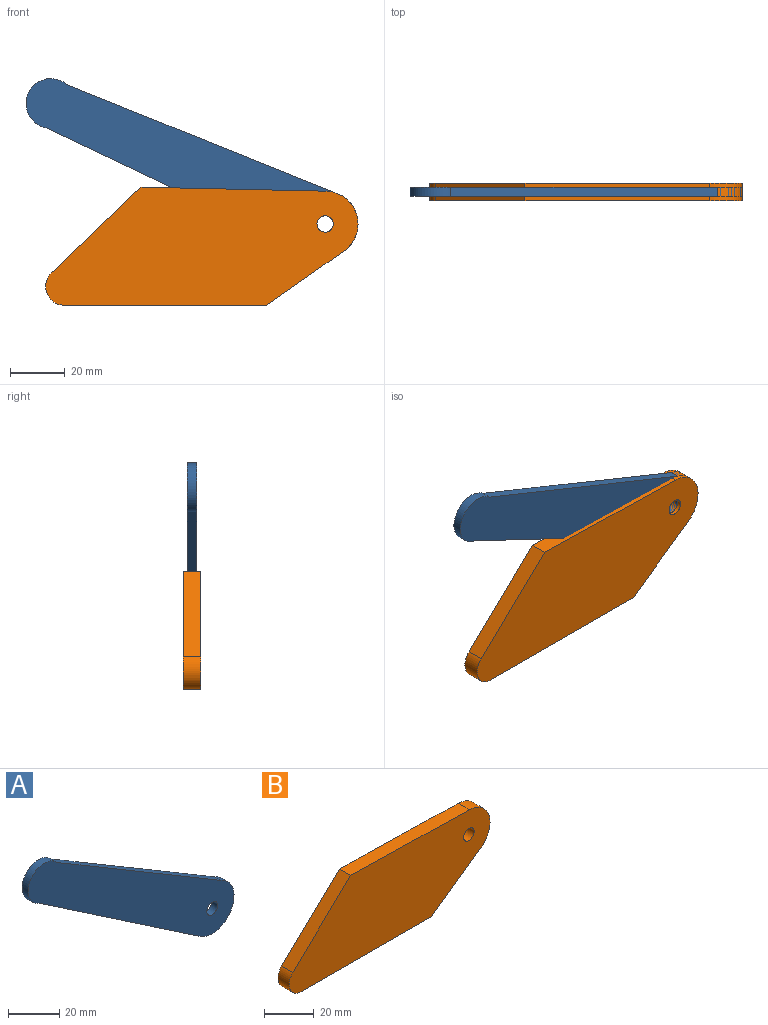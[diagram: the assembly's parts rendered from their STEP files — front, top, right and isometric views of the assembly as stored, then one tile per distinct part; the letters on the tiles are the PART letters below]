
ASSEMBLY  parts=2 mates=1
PART A: 7 faces, bbox 113.4x3.3x79.7 mm
  f0: cylinder r=9.06mm len=17.63mm, axis (0,1,0), area 109.5mm2, adj f1,f3,f5,f6
  f1: plane 88.52x60.05mm, normal (-0.56,0,-0.83), area 353.2mm2, adj f0,f2,f5,f6
  f2: cylinder r=11.99mm len=23.01mm, axis (0,1,0), area 132mm2, adj f1,f3,f5,f6
  f3: plane 90.21x53.63mm, normal (0.51,0,0.86), area 346.5mm2, adj f0,f2,f5,f6
  f4: cylinder r=2.98mm len=5.96mm, axis (0,1,0), area 61.8mm2, adj f5,f6
  f5: plane 113.35x79.74mm, normal (0,-1,0), area 2584.7mm2, adj f0,f1,f2,f3,f4
  f6: plane 113.35x79.74mm, normal (0,1,0), area 2584.7mm2, adj f0,f1,f2,f3,f4
PART B: 9 faces, bbox 114x6.4x43.1 mm
  f0: cylinder r=6.85mm len=11.8mm, axis (0,1,0), area 103.5mm2, adj f1,f5,f7,f8
  f1: plane 73.85x6.35mm, normal (0,0,-1), area 468.9mm2, adj f0,f2,f7,f8
  f2: plane 28.21x19.87mm, normal (0.58,0,-0.82), area 219.1mm2, adj f1,f3,f7,f8
  f3: cylinder r=11.99mm len=21.79mm, axis (0,1,0), area 190.9mm2, adj f2,f4,f7,f8
  f4: plane 67.48x6.35mm, normal (0.02,0,1), area 428.6mm2, adj f3,f5,f7,f8
  f5: plane 32.68x31.31mm, normal (-0.69,0,0.72), area 287.4mm2, adj f0,f4,f7,f8
  f6: cylinder r=2.98mm len=6.35mm, axis (0,1,0), area 118.8mm2, adj f7,f8
  f7: plane 114x43.12mm, normal (0,-1,0), area 3803mm2, adj f0,f1,f2,f3,f4,f5,f6
  f8: plane 114x43.12mm, normal (0,1,0), area 3803mm2, adj f0,f1,f2,f3,f4,f5,f6
PLACE A rot(axis=(0,-1,0),8.7deg) t=(-2.34,0,-8.74)mm
PLACE B at identity fixed
MATE revolute A.f2 <-> B.f3  axis (0,1,0) through (55.97,0,-19.68)mm
